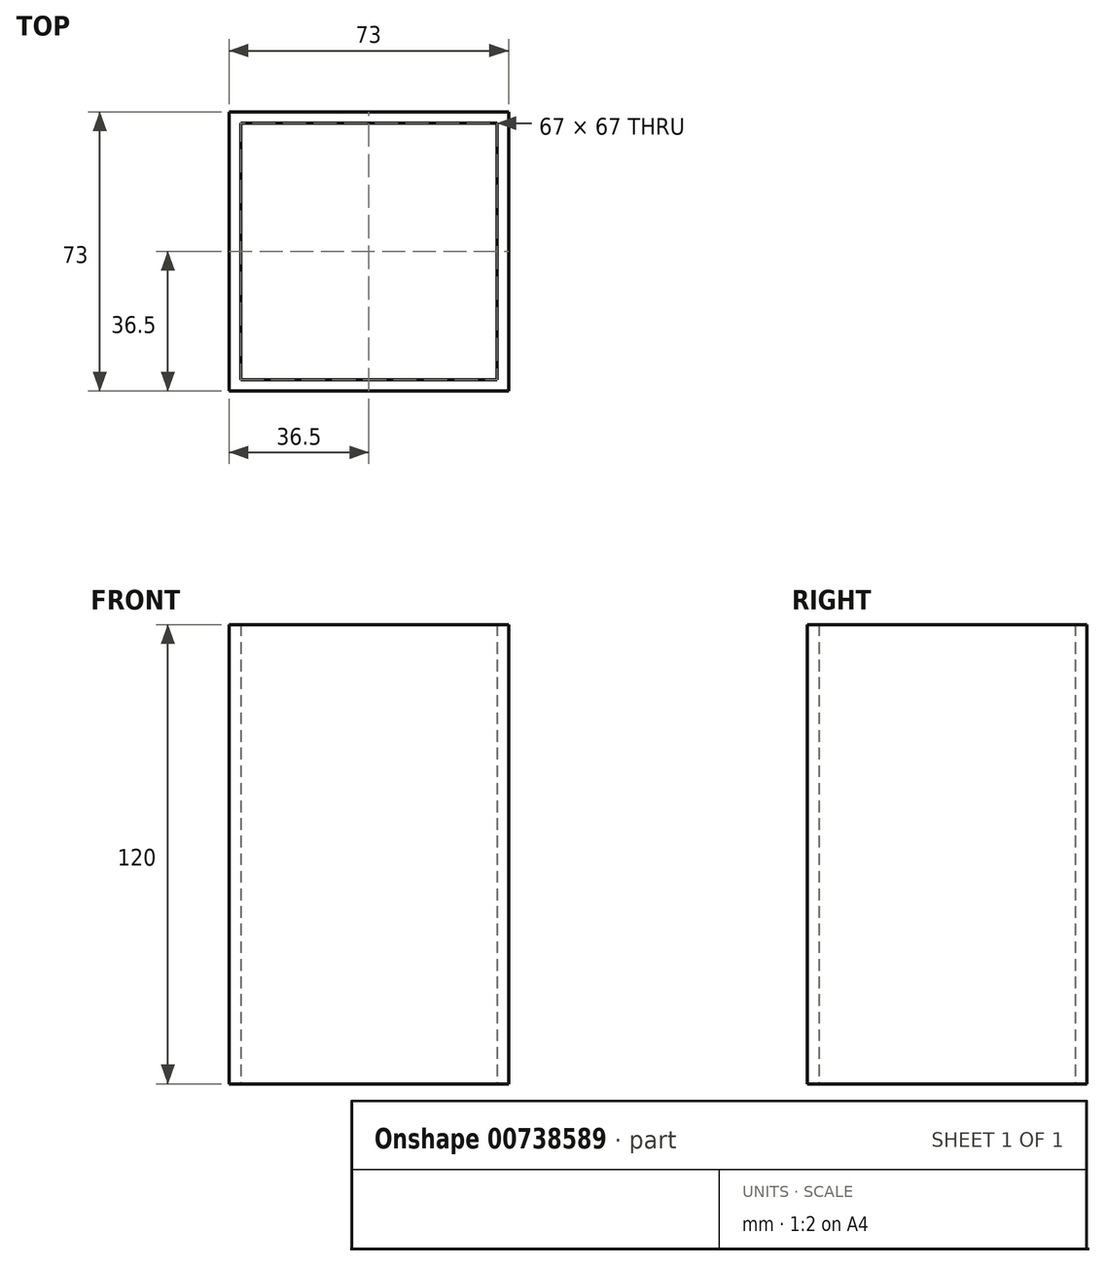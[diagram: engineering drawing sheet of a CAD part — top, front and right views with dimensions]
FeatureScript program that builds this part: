
annotation { "Feature Type Name" : "Feature", "Feature Type Description" : "" }
export const myFeature = defineFeature(function(context is Context, id is Id, definition is map)
    precondition{}
    {
        {
            var Q0;
            Q0=qCreatedBy(makeId("Top.planeOp"),FACE);
            var sketch = newSketch(context, id + "F0", { "sketchPlane" : qUnion([Q0])});
            skLineSegment(sketch, "E0.bottom", {"start": v(0, 0) * mm, "end": v(73, 0) * mm});
            skLineSegment(sketch, "E0.top", {"start": v(0, 73) * mm, "end": v(73, 73) * mm});
            skLineSegment(sketch, "E0.left", {"start": v(0, 0) * mm, "end": v(0, 73) * mm});
            skLineSegment(sketch, "E0.right", {"start": v(73, 0) * mm, "end": v(73, 73) * mm});
            skLineSegment(sketch, "E1.bottom", {"start": v(3, 70) * mm, "end": v(70, 70) * mm});
            skLineSegment(sketch, "E1.top", {"start": v(3, 3) * mm, "end": v(70, 3) * mm});
            skLineSegment(sketch, "E1.left", {"start": v(3, 70) * mm, "end": v(3, 3) * mm});
            skLineSegment(sketch, "E1.right", {"start": v(70, 70) * mm, "end": v(70, 3) * mm});
            skSolve(sketch);
        }
        {
            var Q0;
            Q0 = qSketchRegion(id + "F0", true);
            extrude(context, id + "F1", {"entities" : qUnion([Q0]), "depth" : 120 * mm, "offsetDistance" : 25 * mm});
        }
    });
